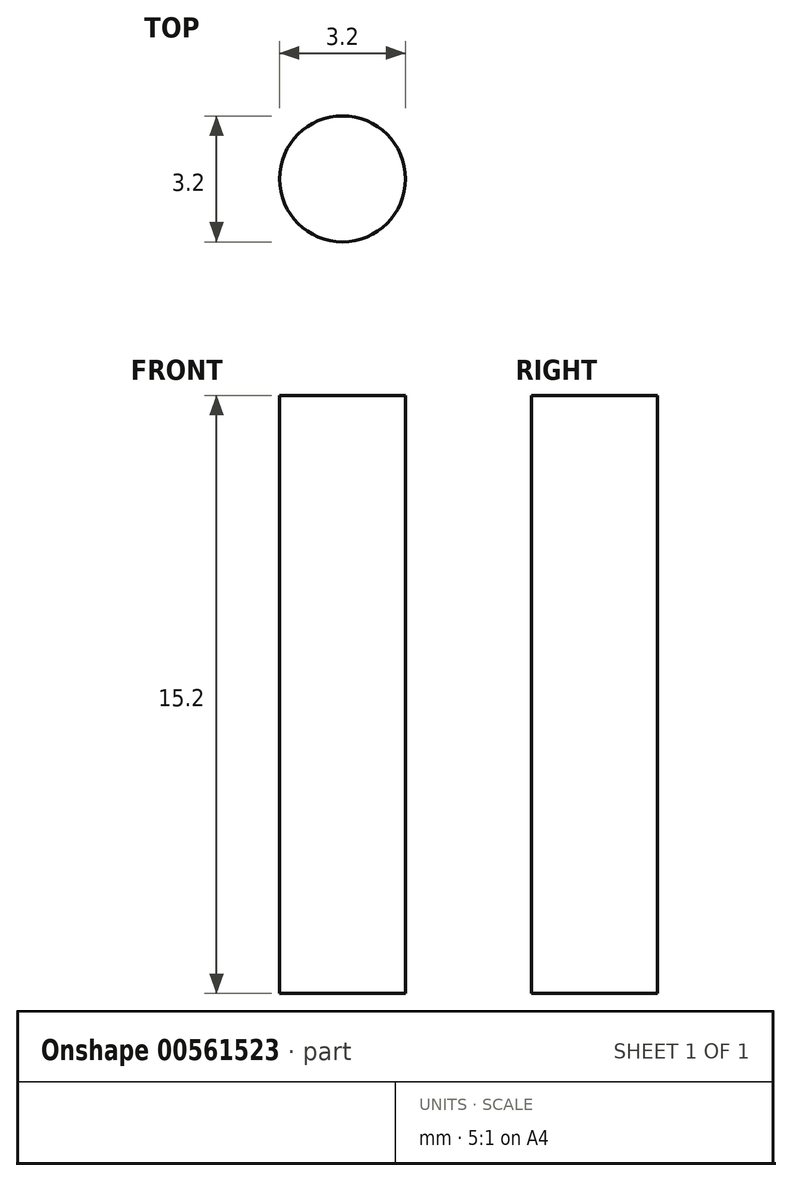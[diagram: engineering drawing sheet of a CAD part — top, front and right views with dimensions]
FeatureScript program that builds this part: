
annotation { "Feature Type Name" : "Feature", "Feature Type Description" : "" }
export const myFeature = defineFeature(function(context is Context, id is Id, definition is map)
    precondition{}
    {
        {
            var Q0;
            Q0=qCreatedBy(makeId("Top.planeOp"),FACE);
            var sketch = newSketch(context, id + "F0", { "sketchPlane" : qUnion([Q0])});
            skCircle(sketch, "E0", {"center": v(0, 0) * mm, "radius": 1.6 * mm});
            skSolve(sketch);
        }
        {
            var Q0;
            Q0 = qSketchRegion(id + "F0", true);
            extrude(context, id + "F1", {"entities" : qUnion([Q0]), "depth" : 15.2 * mm, "offsetDistance" : 25 * mm, "symmetric" : true});
        }
    });
